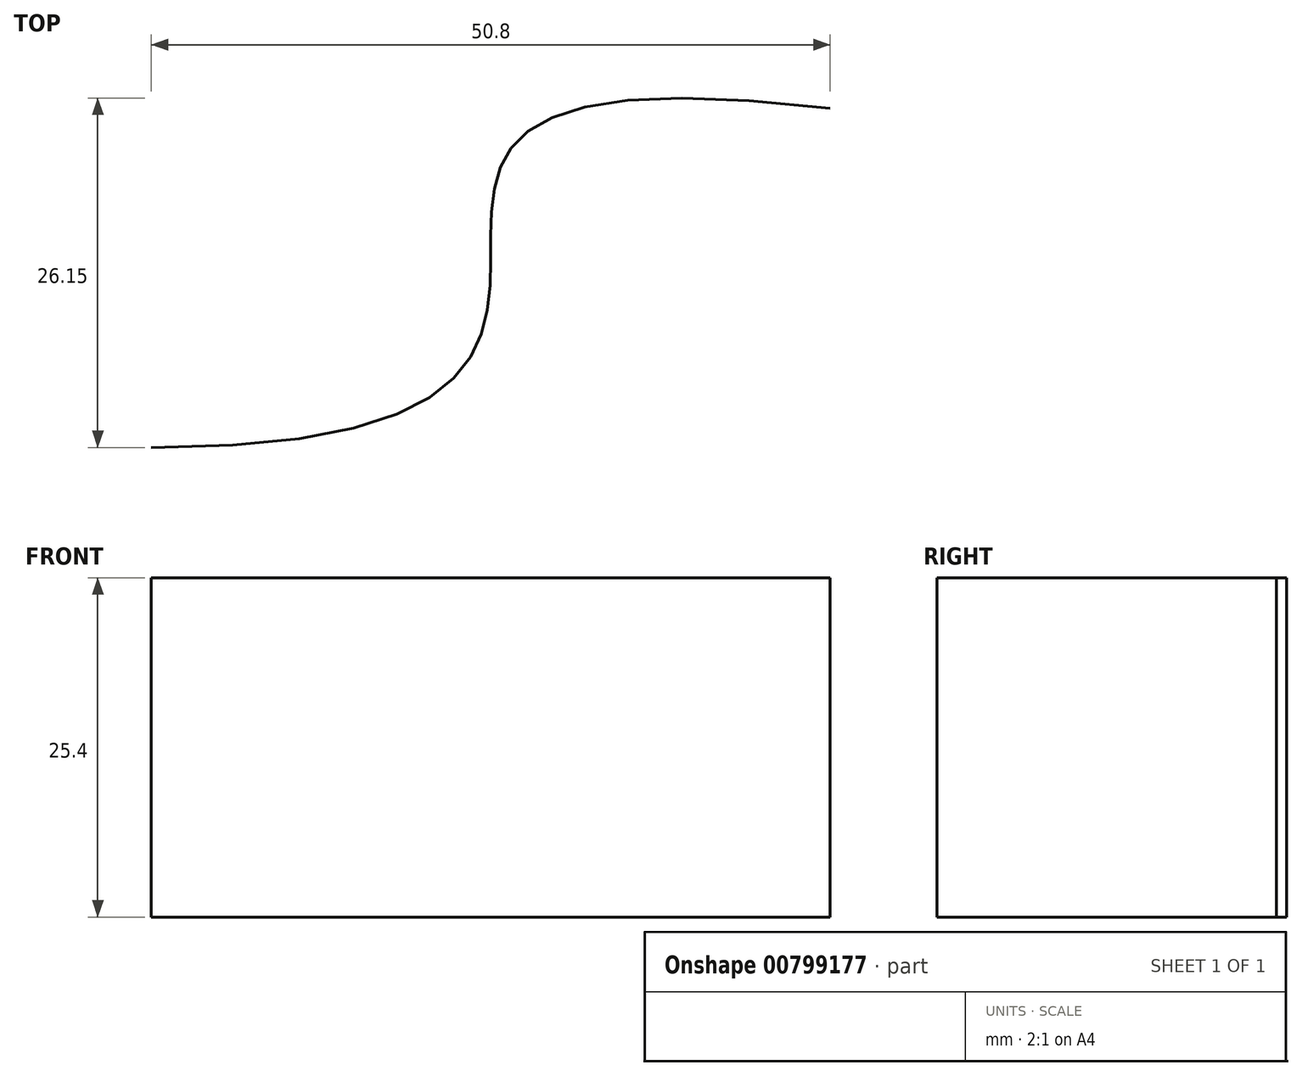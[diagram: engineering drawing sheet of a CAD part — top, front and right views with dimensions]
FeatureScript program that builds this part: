
annotation { "Feature Type Name" : "Feature", "Feature Type Description" : "" }
export const myFeature = defineFeature(function(context is Context, id is Id, definition is map)
    precondition{}
    {
        {
            var Q0;
            Q0=qCreatedBy(makeId("Top.planeOp"),FACE);
            var sketch = newSketch(context, id + "F0", { "sketchPlane" : qUnion([Q0])});
            skFitSpline(sketch, "E0", {"points": [v(0, 0) * mm, v(50.8, 25.4) * mm], "startDerivative": vector(152.4, 0) * mm, "endDerivative": vector(152.4, -17.84) * mm});
            skLineSegment(sketch, "E1", {"start": v(0, 31.35) * mm, "end": v(50.8, 0) * mm, "construction": true});
            skLineSegment(sketch, "E2", {"start": v(0, 31.35) * mm, "end": v(50.8, 25.4) * mm, "construction": true});
            skFitSpline(sketch, "E3", {"points": [v(0, 0) * mm, v(-4, 28.9) * mm], "startDerivative": vector(-44.13, 0) * mm, "endDerivative": vector(19.68, 8.37) * mm});
            skSolve(sketch);
        }
        {
            var Q0;
            Q0=qSketchRegion(id+"F0",true);
            var Q1;
            Q1=sQuery(id+"F0.wireOp",EDGE,"E0");
            extrude(context, id + "F1", {"entities" : qUnion([Q0]), "bodyType" : ToolBodyType.SURFACE, "surfaceEntities" : qUnion([Q1]), "depth" : 25.4 * mm});
        }
    });
